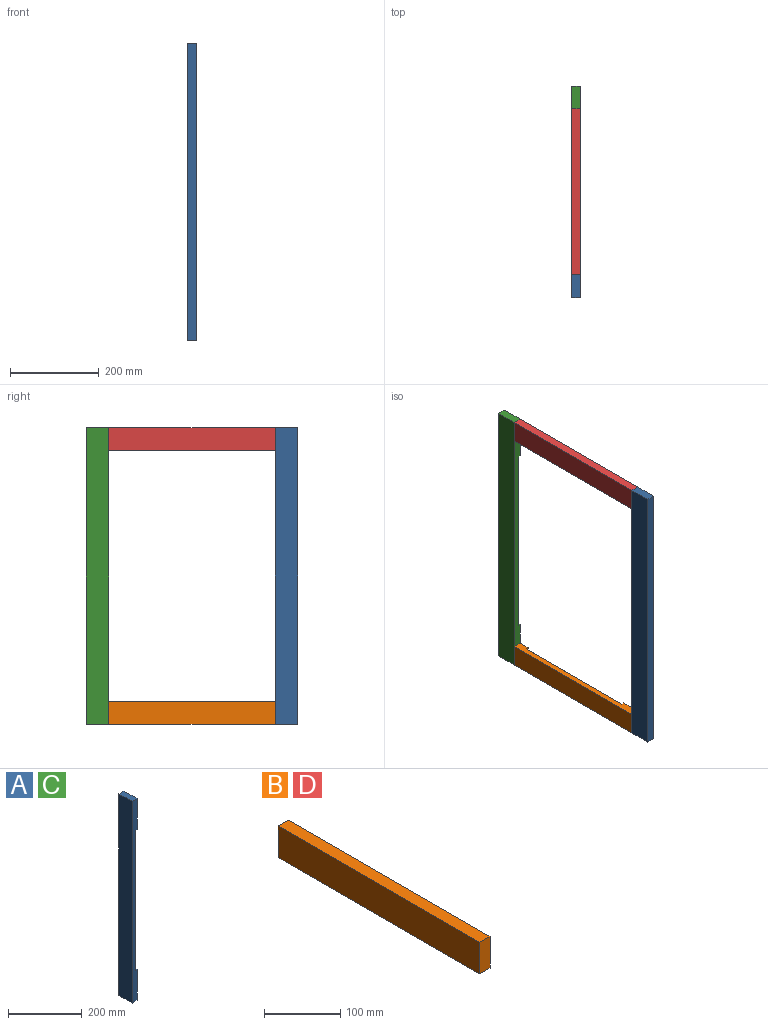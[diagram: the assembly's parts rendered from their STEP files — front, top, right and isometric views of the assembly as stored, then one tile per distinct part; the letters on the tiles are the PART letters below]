
ASSEMBLY  parts=4 mates=10
PART A: 9 faces, bbox 19.1x50.8x669.9 mm
  f0: plane 669.93x19.05mm, normal (0,-1,0), area 9798.4mm2, adj f1,f2,f3,f4,f6,f7,f8
  f1: plane 50.8x19.05mm, normal (0,0,-1), area 967.7mm2, adj f0,f2,f4,f5
  f2: plane 669.93x50.8mm, normal (1,0,0), area 31068.5mm2, adj f0,f1,f3,f5,f6,f7,f8
  f3: plane 50.8x19.05mm, normal (0,0,1), area 967.7mm2, adj f0,f2,f4,f5
  f4: plane 669.93x50.8mm, normal (-1,0,0), area 34032.2mm2, adj f0,f1,f3,f5
  f5: plane 669.93x19.05mm, normal (0,1,0), area 12762.1mm2, adj f1,f2,f3,f4
  f6: plane 466.73x6.35mm, normal (0.71,-0.71,0), area 4191.3mm2, adj f0,f2,f7,f8
  f7: plane 6.35x6.35mm, normal (0,0,-1), area 20.2mm2, adj f0,f2,f6
  f8: plane 6.35x6.35mm, normal (0,0,1), area 20.2mm2, adj f0,f2,f6
PART B: 9 faces, bbox 19.1x374.7x50.8 mm
  f0: plane 374.65x19.05mm, normal (0,0,-1), area 5201.6mm2, adj f1,f2,f3,f4,f6,f7,f8
  f1: plane 374.65x50.8mm, normal (-1,0,0), area 19032.2mm2, adj f0,f2,f4,f5
  f2: plane 50.8x19.05mm, normal (0,1,0), area 967.7mm2, adj f0,f1,f3,f5
  f3: plane 374.65x50.8mm, normal (1,0,0), area 17096.7mm2, adj f0,f2,f4,f5,f6,f7,f8
  f4: plane 50.8x19.05mm, normal (0,-1,0), area 967.7mm2, adj f0,f1,f3,f5
  f5: plane 374.65x19.05mm, normal (0,0,1), area 7137.1mm2, adj f1,f2,f3,f4
  f6: plane 304.8x6.35mm, normal (0.71,0,-0.71), area 2737.2mm2, adj f0,f3,f7,f8
  f7: plane 6.35x6.35mm, normal (0,-1,0), area 20.2mm2, adj f0,f3,f6
  f8: plane 6.35x6.35mm, normal (0,1,0), area 20.2mm2, adj f0,f3,f6
PART C: same geometry as A
PART D: same geometry as B
PLACE A rot(axis=(1,0,0),180deg) t=(-911.15,234.45,-789.1)mm
PLACE B rot(axis=(1,0,0),180deg) t=(-911.15,234.45,-789.1)mm
PLACE C t=(-911.15,-375.15,-119.18)mm
PLACE D t=(-911.15,-375.15,-119.18)mm
MATE planar D.f3 <-> C.f2  axis (1,0,0) through (708.1,-69.28,-142.06)mm
MATE planar D.f5 <-> C.f3  axis (0,0,1) through (698.57,-70.35,-119.18)mm
MATE planar C.f2 <-> A.f2  axis (1,0,0) through (708.1,116.97,-169.98)mm
MATE planar A.f1 <-> C.f3  axis (0,0,1) through (698.57,-283.08,-119.18)mm
MATE planar C.f0 <-> D.f2  axis (0,-1,0) through (696.65,116.97,-454.14)mm
MATE planar B.f4 <-> C.f0  axis (0,1,0) through (698.57,116.97,-763.7)mm
MATE planar B.f2 <-> A.f0  axis (0,-1,0) through (698.57,-257.68,-763.7)mm
MATE planar C.f1 <-> B.f5  axis (0,0,-1) through (698.57,142.37,-789.1)mm
MATE planar C.f2 <-> D.f3  axis (1,0,0) through (708.1,144.49,-454.14)mm
MATE planar B.f3 <-> C.f2  axis (1,0,0) through (708.1,-71.43,-766.22)mm
